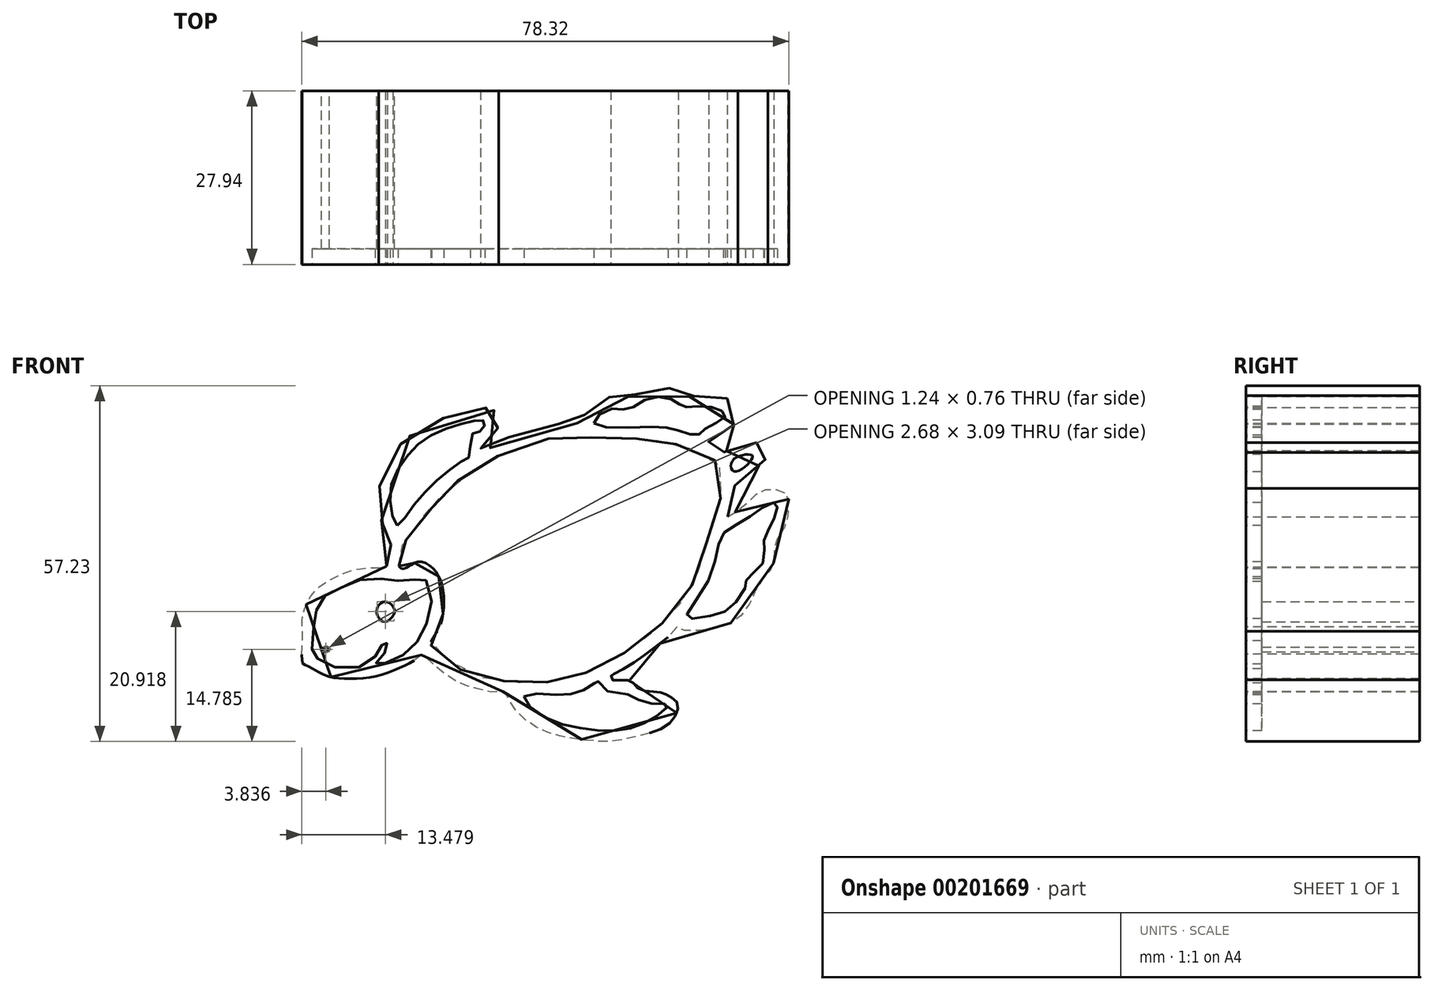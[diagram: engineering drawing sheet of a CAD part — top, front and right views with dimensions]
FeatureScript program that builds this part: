
annotation { "Feature Type Name" : "Feature", "Feature Type Description" : "" }
export const myFeature = defineFeature(function(context is Context, id is Id, definition is map)
    precondition{}
    {
        {
            var Q0;
            Q0=qCreatedBy(makeId("Front.planeOp"),FACE);
            var sketch = newSketch(context, id + "F0", { "sketchPlane" : qUnion([Q0])});
            skLineSegment(sketch, "E0", {"start": v(-741.63, 413) * mm, "end": v(-665.43, 413) * mm});
            skFitSpline(sketch, "E1", {"points": [v(-779.92, 517.97) * mm, v(-779.95, 519.13) * mm, v(-780.11, 519.77) * mm, v(-779.89, 520.73) * mm, v(-779.18, 521.5) * mm, v(-778.92, 521.93) * mm, v(-779.11, 522.4) * mm, v(-779.76, 523.24) * mm, v(-780.63, 524.95) * mm, v(-781.04, 526.82) * mm, v(-781.2, 529.97) * mm, v(-780.53, 532.8) * mm, v(-778.37, 536.82) * mm, v(-774.8, 539.91) * mm, v(-770.78, 541.81) * mm, v(-767.24, 542.84) * mm, v(-764.09, 543.45) * mm, v(-763.06, 543.36) * mm, v(-762.15, 542.3) * mm, v(-761.93, 540.56) * mm, v(-762.48, 539.56) * mm, v(-763.7, 538.47) * mm, v(-764.76, 537.7) * mm, v(-764.67, 536.66) * mm, v(-764.34, 536.57) * mm, v(-762.5, 537.47) * mm, v(-759.45, 539.1) * mm, v(-754.98, 540.46) * mm, v(-750.83, 540.88) * mm, v(-749.57, 540.81) * mm, v(-749.06, 541.3) * mm, v(-747.66, 542.79) * mm, v(-746.17, 543.97) * mm, v(-744.83, 545.07) * mm, v(-743.68, 545.19) * mm, v(-742.04, 545.37) * mm, v(-741.58, 545.25) * mm, v(-740.25, 545.43) * mm, v(-738.67, 546.55) * mm, v(-735.78, 546.98) * mm, v(-734.05, 546.46) * mm, v(-732.69, 546) * mm, v(-731.96, 545.37) * mm, v(-730.74, 545.37) * mm, v(-728.83, 545.37) * mm, v(-726.76, 545.4) * mm, v(-724.73, 544.76) * mm, v(-723.6, 543.55) * mm, v(-723.63, 541.27) * mm, v(-724.51, 540.48) * mm, v(-726.28, 539.36) * mm, v(-727.83, 538.35) * mm, v(-728.16, 537.93) * mm, v(-727.76, 537.5) * mm, v(-727.25, 537.23) * mm, v(-726.28, 536.65) * mm, v(-725.82, 536.29) * mm, v(-724.88, 536.8) * mm, v(-722.3, 537.44) * mm, v(-720.48, 537.84) * mm, v(-719.53, 537.84) * mm, v(-718.93, 537.35) * mm, v(-718.62, 535.92) * mm, v(-719.53, 534.62) * mm, v(-722.51, 532.1) * mm, v(-723.94, 530.94) * mm, v(-724.24, 529.58) * mm, v(-724.93, 526.79) * mm, v(-725.09, 525.9) * mm, v(-724.28, 526.38) * mm, v(-722.09, 528) * mm, v(-720.75, 529.38) * mm, v(-719.61, 530.03) * mm, v(-718, 530.48) * mm, v(-716.61, 530.03) * mm, v(-715.4, 529.46) * mm, v(-715.4, 527.35) * mm, v(-715.4, 525.93) * mm, v(-715.88, 524.43) * mm, v(-717.18, 522.29) * mm, v(-717.38, 522) * mm, v(-717.67, 519.7) * mm, v(-717.75, 518.27) * mm, v(-718.52, 516.93) * mm, v(-719.7, 515.6) * mm, v(-720.8, 513.7) * mm, v(-722.13, 510.93) * mm, v(-723.95, 509.2) * mm, v(-725.94, 508.3) * mm, v(-729.02, 507.7) * mm, v(-732.22, 507.7) * mm, v(-733.07, 508.22) * mm, v(-734, 507.24) * mm, v(-736.76, 504.97) * mm, v(-739.76, 502.74) * mm, v(-743.54, 500.55) * mm, v(-743.82, 500.4) * mm, v(-743.7, 499.74) * mm, v(-742.08, 499.66) * mm, v(-740.41, 499.34) * mm, v(-739.4, 498.28) * mm, v(-737.05, 497.8) * mm, v(-735.51, 497.58) * mm, v(-734.35, 497.02) * mm, v(-733.2, 496) * mm, v(-733.28, 494.32) * mm, v(-735.3, 492.08) * mm, v(-739.8, 490.58) * mm, v(-743.98, 489.8) * mm, v(-749.09, 490.15) * mm, v(-753.34, 491.01) * mm, v(-757.3, 493.03) * mm, v(-760, 496) * mm, v(-761.03, 497.75) * mm, v(-762.27, 497.71) * mm, v(-766.74, 498.66) * mm, v(-769.88, 500.16) * mm, v(-773.96, 503.68) * mm, v(-774.13, 503.85) * mm, v(-775.16, 503.04) * mm, v(-778.25, 501.45) * mm, v(-782.38, 500.12) * mm, v(-786.8, 499.9) * mm, v(-789.8, 500.42) * mm, v(-792.9, 502.05) * mm, v(-793.47, 502.4) * mm, v(-793.47, 506.95) * mm, v(-793.47, 509.82) * mm, v(-791.7, 513.78) * mm, v(-788.6, 516.01) * mm, v(-785.43, 517.34) * mm, v(-781.26, 517.77) * mm, v(-779.92, 517.97) * mm]});
            skPoint(sketch, "E2.20.internal.snap0", {"position": v(-793.47, 510.15) * mm});
            skFitSpline(sketch, "E2", {"points": [v(-791.25, 510.86) * mm, v(-791.66, 508.6) * mm, v(-791.9, 505.02) * mm, v(-791.86, 503.73) * mm, v(-790.93, 503.04) * mm, v(-788.13, 501.7) * mm, v(-783.83, 501.94) * mm, v(-781.73, 503.56) * mm, v(-780.8, 504.82) * mm, v(-780.51, 505.67) * mm, v(-779.92, 505.96) * mm, v(-779.92, 505.47) * mm, v(-779.92, 504.54) * mm, v(-780.3, 503.93) * mm, v(-781.24, 502.67) * mm, v(-781.77, 502.27) * mm, v(-781, 502.27) * mm, v(-778.44, 503) * mm, v(-776.21, 504.66) * mm, v(-774.43, 506.73) * mm, v(-773.13, 510.15) * mm, v(-772.85, 514.19) * mm, v(-774.3, 516.25) * mm, v(-775.11, 515.94) * mm, v(-777.46, 515.54) * mm, v(-779.13, 515.88) * mm, v(-782.1, 515.94) * mm, v(-785.5, 515.48) * mm, v(-787.96, 514.1) * mm, v(-790.2, 512.96) * mm, v(-791.25, 510.86) * mm]});
            skFitSpline(sketch, "E3", {"points": [v(-780.91, 512.04) * mm, v(-781.45, 511.22) * mm, v(-781.4, 510.03) * mm, v(-780.42, 509.06) * mm, v(-779.07, 509.82) * mm, v(-778.75, 511.17) * mm, v(-779.92, 512.25) * mm, v(-780.91, 512.04) * mm]});
            skFitSpline(sketch, "E4", {"points": [v(-777.96, 517.97) * mm, v(-778.07, 519.7) * mm, v(-777.38, 521.38) * mm, v(-774.1, 525.9) * mm, v(-772.4, 527.66) * mm, v(-770.44, 530.05) * mm, v(-765.64, 533.66) * mm, v(-760.62, 536.37) * mm, v(-753.29, 538.6) * mm, v(-749.03, 538.68) * mm, v(-742.92, 538.71) * mm, v(-738.51, 538.43) * mm, v(-734.32, 537.88) * mm, v(-729.95, 536.44) * mm, v(-726.27, 534.08) * mm, v(-726, 529.89) * mm, v(-727.32, 525.3) * mm, v(-729.46, 518.6) * mm, v(-730.92, 514.69) * mm, v(-734.7, 509.68) * mm, v(-739.52, 505.5) * mm, v(-744.16, 502.58) * mm, v(-748.35, 500.67) * mm, v(-752.13, 499.62) * mm, v(-757.36, 499.21) * mm, v(-761.87, 499.62) * mm, v(-767.2, 500.9) * mm, v(-770.97, 503.63) * mm, v(-772.85, 505.45) * mm, v(-771.7, 507.7) * mm, v(-770.74, 511.64) * mm, v(-771.2, 515.48) * mm, v(-772.85, 517.97) * mm, v(-774.84, 518.7) * mm, v(-776.39, 517.97) * mm, v(-776.98, 517.65) * mm, v(-777.39, 517.55) * mm, v(-777.96, 517.97) * mm]});
            skFitSpline(sketch, "E5", {"points": [v(-790.38, 504.32) * mm, v(-790.2, 504.84) * mm, v(-789.53, 504.94) * mm, v(-789.15, 504.77) * mm, v(-789.33, 504.35) * mm, v(-790.38, 504.32) * mm]});
            skFitSpline(sketch, "E6", {"points": [v(-778.25, 524.56) * mm, v(-779.13, 526.6) * mm, v(-779.13, 531.31) * mm, v(-776.61, 535.7) * mm, v(-773.54, 538.6) * mm, v(-769.21, 540.52) * mm, v(-765.77, 541.37) * mm, v(-764.4, 541.44) * mm, v(-764.13, 540.96) * mm, v(-764.47, 540.04) * mm, v(-765.36, 539.53) * mm, v(-766.28, 539.1) * mm, v(-766.55, 535.74) * mm, v(-767.2, 535.27) * mm, v(-769.65, 533.6) * mm, v(-773.44, 530.29) * mm, v(-776.5, 526.54) * mm, v(-778.25, 524.56) * mm]});
            skFitSpline(sketch, "E7", {"points": [v(-725.67, 523.39) * mm, v(-726.67, 520.8) * mm, v(-728.54, 515.01) * mm, v(-731.68, 510.15) * mm, v(-731.45, 509.6) * mm, v(-727.13, 510.15) * mm, v(-724.53, 511.37) * mm, v(-722.26, 514.6) * mm, v(-722.16, 515.48) * mm, v(-721.07, 516.88) * mm, v(-719.39, 518.56) * mm, v(-719.25, 521.2) * mm, v(-719.2, 522.29) * mm, v(-718.43, 524.03) * mm, v(-717.18, 526.79) * mm, v(-717.18, 527.9) * mm, v(-717.67, 528.21) * mm, v(-719.57, 527.35) * mm, v(-722.71, 525.16) * mm, v(-725.67, 523.39) * mm]});
            skFitSpline(sketch, "E8", {"points": [v(-757.82, 497.05) * mm, v(-752.9, 497.3) * mm, v(-749.13, 497.72) * mm, v(-746.52, 499.18) * mm, v(-746.15, 499.62) * mm, v(-744.16, 497.72) * mm, v(-742.26, 497.66) * mm, v(-740.02, 496.75) * mm, v(-736.92, 495.84) * mm, v(-734.7, 495.66) * mm, v(-735.76, 494.44) * mm, v(-739.04, 492.5) * mm, v(-743.54, 491.52) * mm, v(-749.2, 492.01) * mm, v(-755.02, 494.02) * mm, v(-757.82, 497.05) * mm]});
            skFitSpline(sketch, "E9", {"points": [v(-746.6, 541) * mm, v(-744.16, 543.22) * mm, v(-741.12, 543.26) * mm, v(-737.44, 545.1) * mm, v(-733.5, 544.52) * mm, v(-732.2, 543.68) * mm, v(-729.02, 543.72) * mm, v(-725.77, 542.79) * mm, v(-725.62, 541.84) * mm, v(-728.72, 540.12) * mm, v(-729.87, 539.1) * mm, v(-733.04, 539.81) * mm, v(-737.52, 540.39) * mm, v(-746.6, 541) * mm]});
            skFitSpline(sketch, "E10", {"points": [v(-724.35, 534.9) * mm, v(-723.95, 533.2) * mm, v(-721.1, 535.4) * mm, v(-721.39, 535.92) * mm, v(-724.35, 534.9) * mm]});
            skSolve(sketch);
        }
        {
            var Q0;
            Q0=makeQuery(id+"F0.imprint","IMPRINT",FACE,{"disambiguationData":[TD([[makeQuery(id+"F0.imprint","IMPRINT",EDGE,{"derivedFrom":sQuery(id+"F0.wireOp",EDGE,"E2")}),1.0]])]});
            var Q1;
            Q1=makeQuery(id+"F0.imprint","IMPRINT",FACE,{"disambiguationData":[TD([[makeQuery(id+"F0.imprint","IMPRINT",EDGE,{"derivedFrom":sQuery(id+"F0.wireOp",EDGE,"E4")}),-1.0]])]});
            var Q2;
            Q2=makeQuery(id+"F0.imprint","IMPRINT",FACE,{"disambiguationData":[TD([[makeQuery(id+"F0.imprint","IMPRINT",EDGE,{"derivedFrom":sQuery(id+"F0.wireOp",EDGE,"E8")}),-1.0]])]});
            var Q3;
            Q3=makeQuery(id+"F0.imprint","IMPRINT",FACE,{"disambiguationData":[TD([[makeQuery(id+"F0.imprint","IMPRINT",EDGE,{"derivedFrom":sQuery(id+"F0.wireOp",EDGE,"E7")}),1.0]])]});
            var Q4;
            Q4=makeQuery(id+"F0.imprint","IMPRINT",FACE,{"disambiguationData":[TD([[makeQuery(id+"F0.imprint","IMPRINT",EDGE,{"derivedFrom":sQuery(id+"F0.wireOp",EDGE,"E9")}),-1.0]])]});
            var Q5;
            Q5=makeQuery(id+"F0.imprint","IMPRINT",FACE,{"disambiguationData":[TD([[makeQuery(id+"F0.imprint","IMPRINT",EDGE,{"derivedFrom":sQuery(id+"F0.wireOp",EDGE,"E10")}),1.0]])]});
            var Q6;
            Q6=makeQuery(id+"F0.imprint","IMPRINT",FACE,{"disambiguationData":[TD([[makeQuery(id+"F0.imprint","IMPRINT",EDGE,{"derivedFrom":sQuery(id+"F0.wireOp",EDGE,"E6")}),-1.0]])]});
            var Q7;
            Q7=makeQuery(id+"F0.imprint","IMPRINT",FACE,{"disambiguationData":[TD([[makeQuery(id+"F0.imprint","IMPRINT",EDGE,{"derivedFrom":sQuery(id+"F0.wireOp",EDGE,"E1")}),-1.0]])]});
            extrude(context, id + "F1", {"entities" : qUnion([Q0, Q1, Q2, Q3, Q4, Q5, Q6, Q7]), "depth" : 25.4 * mm});
        }
        {
            var Q0;
            Q0=makeQuery(id+"F0.imprint","IMPRINT",FACE,{"disambiguationData":[TD([[makeQuery(id+"F0.imprint","IMPRINT",EDGE,{"derivedFrom":sQuery(id+"F0.wireOp",EDGE,"E1")}),-1.0]])]});
            extrude(context, id + "F2", {"entities" : qUnion([Q0]), "operationType" : NewBodyOperationType.ADD, "depth" : 27.94 * mm});
        }
    });
